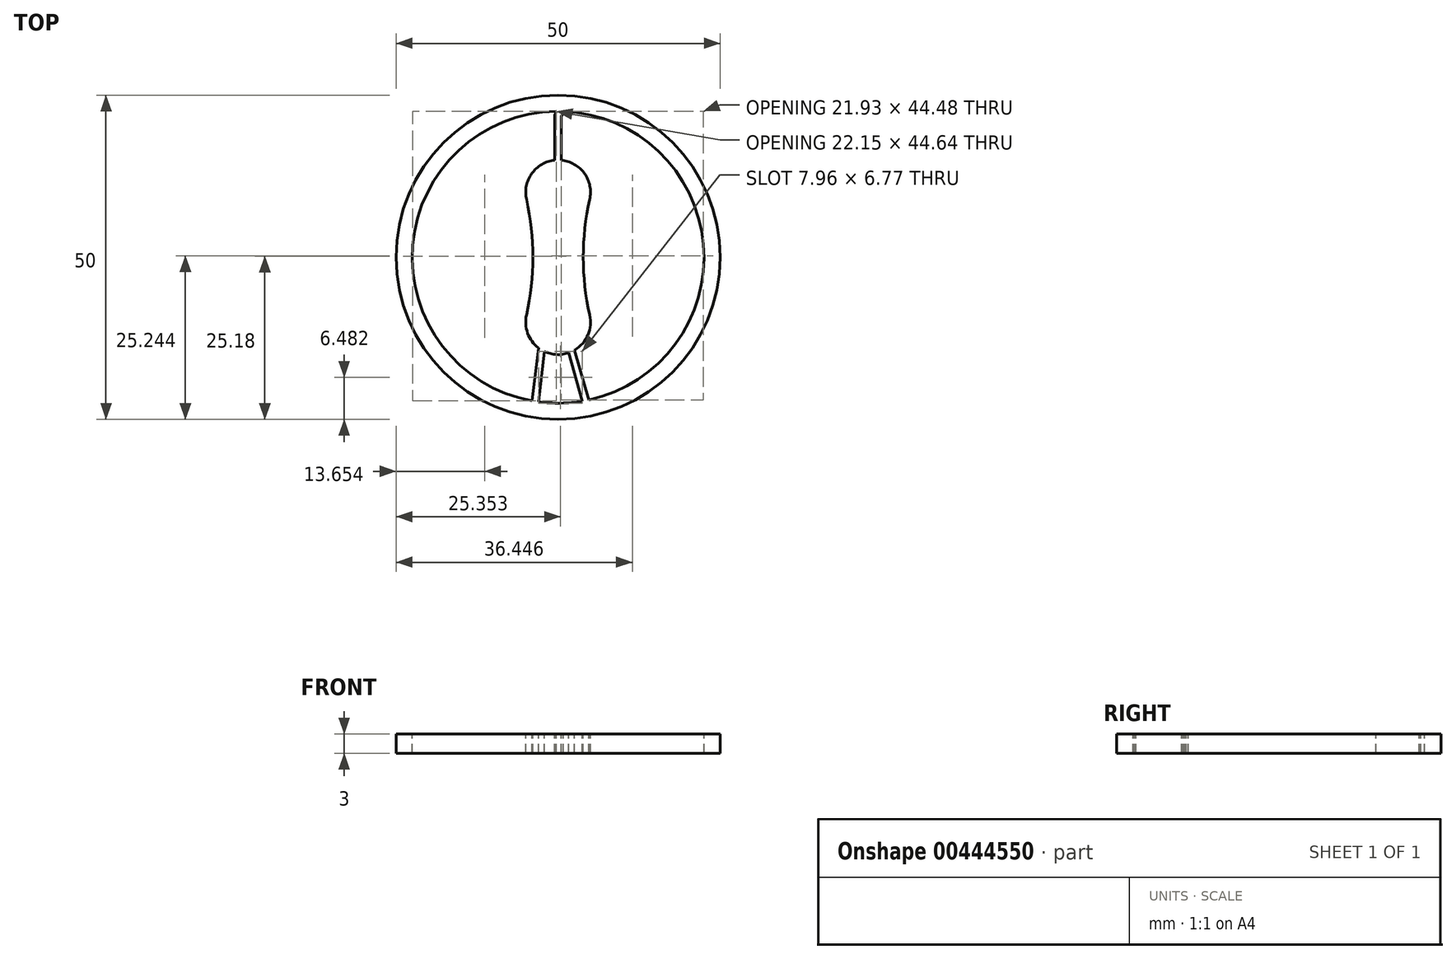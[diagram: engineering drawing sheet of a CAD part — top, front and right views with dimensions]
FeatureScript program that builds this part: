
annotation { "Feature Type Name" : "Feature", "Feature Type Description" : "" }
export const myFeature = defineFeature(function(context is Context, id is Id, definition is map)
    precondition{}
    {
        {
            var Q0;
            Q0=qCreatedBy(makeId("Top.planeOp"),FACE);
            var sketch = newSketch(context, id + "F0", { "sketchPlane" : qUnion([Q0])});
            skPoint(sketch, "E0.middle", {"position": v(0, 0) * mm});
            skCircle(sketch, "E1", {"center": v(0, 0) * mm, "radius": 25 * mm});
            skPoint(sketch, "E2.orphan", {"position": v(-25, 25) * mm});
            skPoint(sketch, "E3.orphan", {"position": v(25, 25) * mm});
            skPoint(sketch, "E4.orphan", {"position": v(25, -25) * mm});
            skPoint(sketch, "E0.right.end.orphan", {"position": v(-25, -25) * mm});
            skSolve(sketch);
        }
        {
            var Q0;
            Q0 = qSketchRegion(id + "F0", true);
            extrude(context, id + "F1", {"entities" : qUnion([Q0]), "depth" : 3 * mm});
        }
        {
            var Q0;
            Q0=makeQuery(id+"F1.opExtrude","CAP_FACE",FACE,{"disambiguationData":[OSD([sQuery(id+"F0.wireOp",EDGE,"E1")])],"isStart":false});
            var sketch = newSketch(context, id + "F2", { "sketchPlane" : qUnion([Q0])});
            skCircle(sketch, "E5", {"center": v(0, 0) * mm, "radius": 22.5 * mm});
            skCircle(sketch, "E6", {"center": v(0, 10) * mm, "radius": 5 * mm});
            skCircle(sketch, "E7", {"center": v(0, -10) * mm, "radius": 5 * mm});
            skArc(sketch, "E8", {"start": v(-14.1, -26.7) * mm, "mid": v(-11.63, -23.67) * mm, "end": v(-9.47, -20.4) * mm});
            skArc(sketch, "E9.trimOffspring", {"start": v(4.87, 8.89) * mm, "mid": v(3.87, 0) * mm, "end": v(4.87, -8.89) * mm});
            skArc(sketch, "E10.trimOffspring", {"start": v(-4.87, -8.89) * mm, "mid": v(-3.87, 0) * mm, "end": v(-4.87, 8.89) * mm});
            skLineSegment(sketch, "E11", {"start": v(-3.03, -13.97) * mm, "end": v(-4.02, -22.14) * mm});
            skLineSegment(sketch, "E12", {"start": v(2.55, -14.3) * mm, "end": v(4.73, -22) * mm});
            skLineSegment(sketch, "E13", {"start": v(-2.1, -14.54) * mm, "end": v(-3.03, -22.3) * mm});
            skLineSegment(sketch, "E14", {"start": v(1.63, -14.73) * mm, "end": v(3.74, -22.19) * mm});
            skLineSegment(sketch, "E15", {"start": v(-0.52, 14.97) * mm, "end": v(-0.52, 21.89) * mm});
            skLineSegment(sketch, "E16", {"start": v(-0.52, 21.89) * mm, "end": v(-0.27, 22.5) * mm});
            skLineSegment(sketch, "E17", {"start": v(0.48, 14.98) * mm, "end": v(0.48, 21.7) * mm});
            skLineSegment(sketch, "E18", {"start": v(0.48, 21.7) * mm, "end": v(0.8, 22.49) * mm});
            skSolve(sketch);
        }
        {
            var Q0;
            {var subQ3=sQuery(id+"F2.wireOp",EDGE,"E9.trimOffspring");Q0=makeQuery(id+"F2.imprint","IMPRINT",FACE,{"disambiguationData":[TD([[makeQuery(id+"F2.imprint","IMPRINT",EDGE,{"derivedFrom":subQ3}),1.0]])]});}
            var Q1;
            {var subQ0=sQuery(id+"F2.wireOp",EDGE,"E13");Q1=makeQuery(id+"F2.imprint","IMPRINT",FACE,{"disambiguationData":[TD([[makeQuery(id+"F2.imprint","IMPRINT",EDGE,{"derivedFrom":subQ0}),1.0]])]});}
            var Q2;
            {var subQ0=sQuery(id+"F2.wireOp",EDGE,"E10.trimOffspring");Q2=makeQuery(id+"F2.imprint","IMPRINT",FACE,{"disambiguationData":[TD([[makeQuery(id+"F2.imprint","IMPRINT",EDGE,{"derivedFrom":subQ0}),1.0]])]});}
            extrude(context, id + "F3", {"entities" : qUnion([Q0, Q1, Q2]), "operationType" : NewBodyOperationType.REMOVE, "oppositeDirection" : true, "depth" : 3 * mm});
        }
    });
